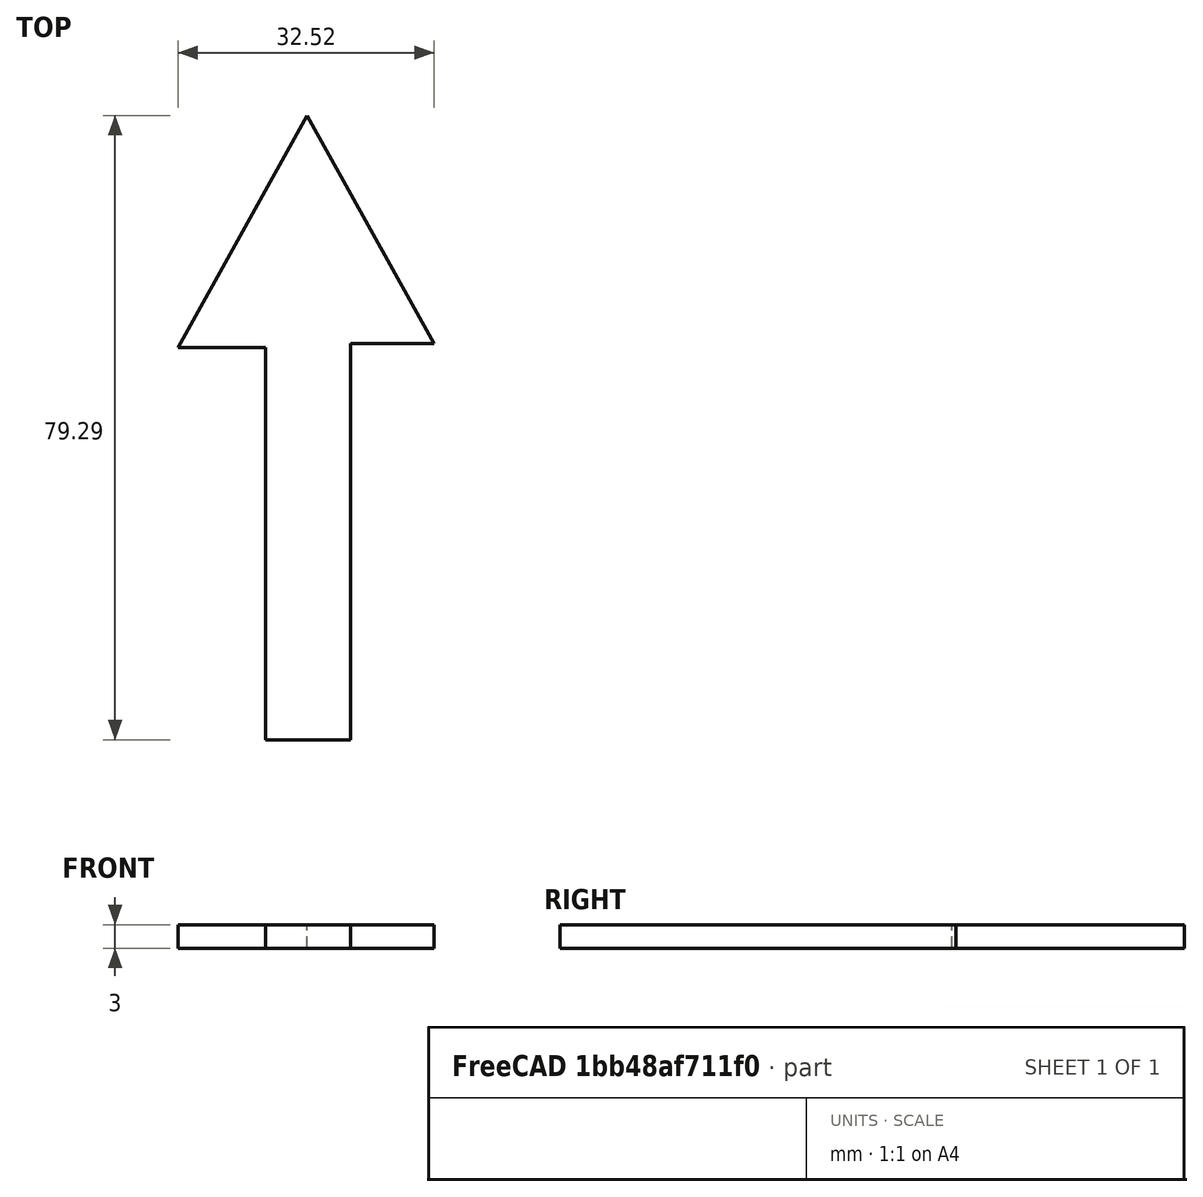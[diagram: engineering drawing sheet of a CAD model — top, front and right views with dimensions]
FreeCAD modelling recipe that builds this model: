
FCSTD DOCUMENT  (FreeCAD 0.21R33694 (Git))
Label: OJT1_T16R02_fletxa
License: All rights reserved
LicenseURL: http://en.wikipedia.org/wiki/All_rights_reserved
objects: Sketcher::SketchObject×1, PartDesign::Pad×1, PartDesign::Body×1
note: 4 computed .brp shape members not serialized (recipe doc carries the construction recipe); baked Part::Feature solids carry a one-line shape summary decoded from their .brp

FEATURE [Sketcher::SketchObject] Sketch
  FullyConstrained = false
  MapMode = 5
  Support = -> [XY_Plane]
  sketch-geometry (7):
    g0: LineSegment StartX=0 StartY=49.3939 StartZ=0 EndX=-16.3636 EndY=19.899 EndZ=0
    g1: LineSegment StartX=-16.3636 StartY=19.899 StartZ=0 EndX=-5.25252 EndY=19.899 EndZ=0
    g2: LineSegment StartX=-5.25252 StartY=19.899 StartZ=0 EndX=-5.25252 EndY=-29.9006 EndZ=0
    g3: LineSegment StartX=-5.25252 StartY=-29.9006 StartZ=0 EndX=5.56052 EndY=-29.9006 EndZ=0
    g4: LineSegment StartX=5.56052 StartY=-29.9006 StartZ=0 EndX=5.56052 EndY=20.4024 EndZ=0
    g5: LineSegment StartX=5.56052 StartY=20.4024 StartZ=0 EndX=16.1616 EndY=20.4024 EndZ=0
    g6: LineSegment StartX=16.1616 StartY=20.4024 StartZ=0 EndX=0 EndY=49.3939 EndZ=0
  constraints (12):
    c: PointOnObject(g0,g-2)
    c: Coincident(g0,g1)
    c: Horizontal(g1)
    c: Coincident(g1,g2)
    c: Vertical(g2)
    c: Coincident(g2,g3)
    c: Horizontal(g3)
    c: Coincident(g3,g4)
    c: Vertical(g4)
    c: Coincident(g4,g5)
    c: Horizontal(g5)
    c: Coincident(g5,g6)
FEATURE [PartDesign::Pad] Pad
  Direction = (0,0,1)
  Length = 3
  Length2 = 10
  Profile = -> Sketch
  ReferenceAxis = -> Sketch [N_Axis]
  Type = 0
FEATURE [PartDesign::Body] Body
  Group = -> [Sketch,Pad]
  Origin = -> Origin
  Tip = -> Pad
